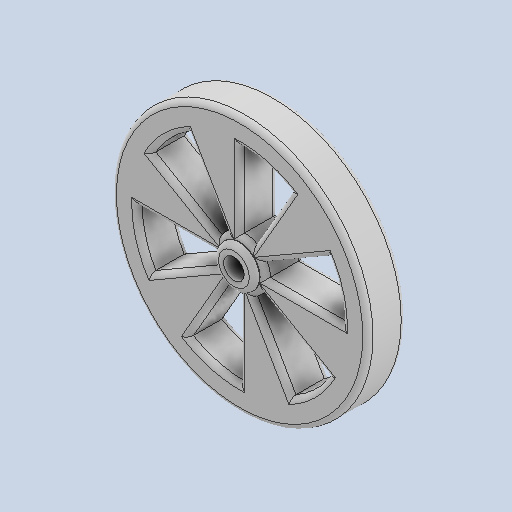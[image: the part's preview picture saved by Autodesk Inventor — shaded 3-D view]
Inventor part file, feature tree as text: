
AUTODESK INVENTOR PART (.ipt)
format: ipt  version: 2022 (Build 260153000, 153)  size: 329,728 bytes
history: native  units: mm
features: extrude x4, sketch x4, fillet x2, pattern_circular x1
ambient origin geometry x8: Origin, YZ Plane, XZ Plane, XY Plane, X Axis, Y Axis, Z Axis, Center Point
bodies: Solid1 (feature_tree)
feature tree (11):
  extrude  "Extrusion1"  Depth=15.0mm TaperAngle=0.0deg
  extrude  "Extrusion2"  Depth=20.0mm
  pattern_circular  "Circular Pattern1"  Count=4  [1 undecoded]
  fillet  "Fillet1"  [1 undecoded]
  extrude  "Extrusion3"  Depth=2.0mm TaperAngle=360.0deg
  fillet  "Fillet2"  Radius=2.0mm
  extrude  "Extrusion4"  Depth=2.0mm
  sketch  "Sketch1"  dims[d0=100.0mm d1=15.0mm d2=0.0mm]
  sketch  "Sketch2"  dims[d3=80.0mm d4=20.0mm d5=40.0mm d6=30.0deg]
  sketch  "Sketch3"  dims[d7=15.0mm d8=0.0mm d9=60.0mm d10=360.0deg d12=2.0mm]
  sketch  "Sketch4"  dims[d13=2.2mm d14=0.0mm d15=2.0mm d16=8.0mm d17=0.0mm d18=0.0mm]
note: 2 required parameter values undecoded (feature->parameter linkage not recoverable at this tier; creation-order binding heuristic only, values carry confidence <= 0.55)
